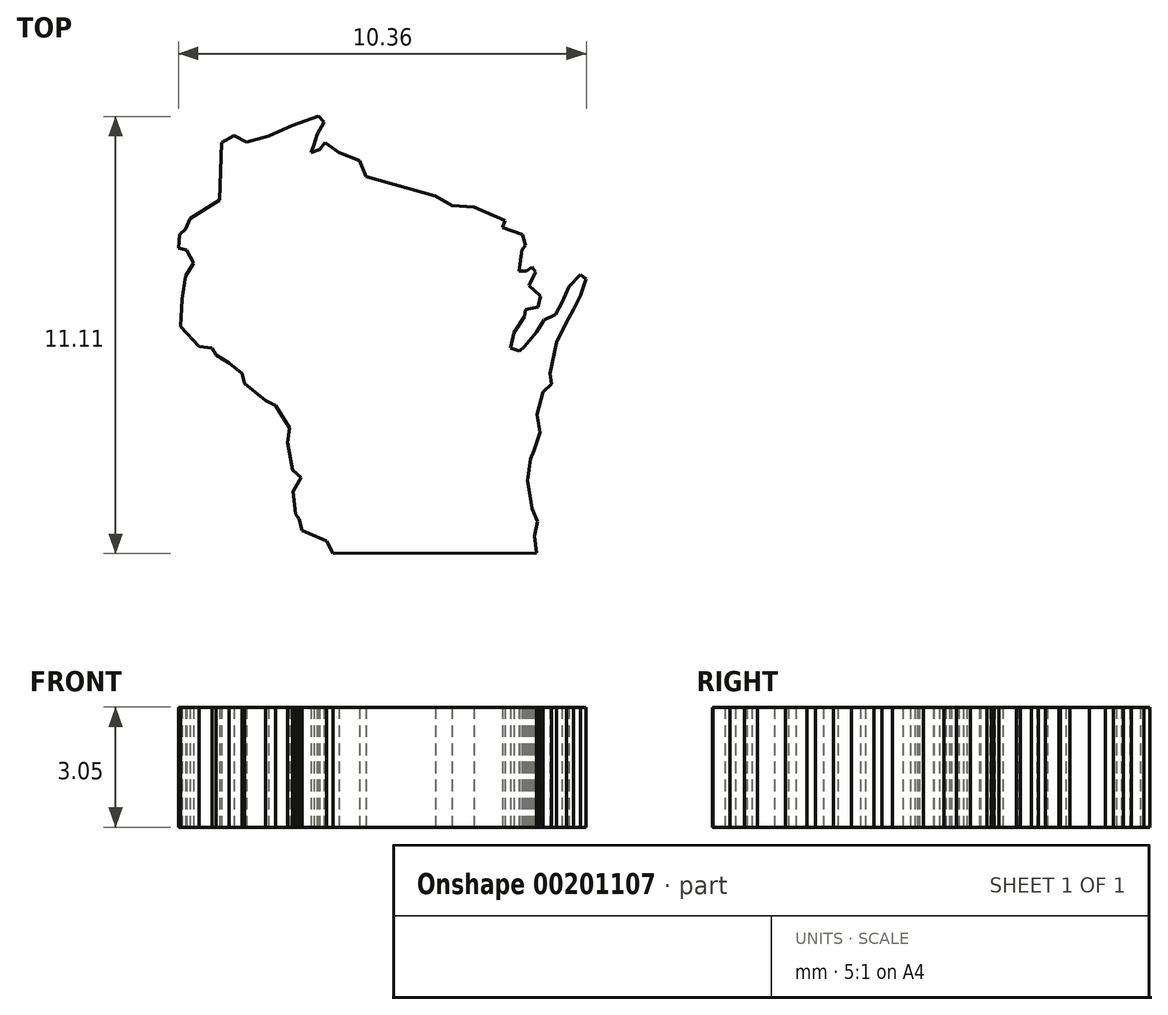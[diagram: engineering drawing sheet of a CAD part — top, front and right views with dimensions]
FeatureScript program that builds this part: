
annotation { "Feature Type Name" : "Feature", "Feature Type Description" : "" }
export const myFeature = defineFeature(function(context is Context, id is Id, definition is map)
    precondition{}
    {
        {
            var Q0;
            Q0=qCreatedBy(makeId("Top.planeOp"),FACE);
            var sketch = newSketch(context, id + "F0", { "sketchPlane" : qUnion([Q0])});
            skLineSegment(sketch, "E0", {"start": v(0.02, 0.02) * mm, "end": v(5.18, 0.03) * mm});
            skLineSegment(sketch, "E1", {"start": v(5.18, 0.03) * mm, "end": v(5.14, 0.47) * mm});
            skLineSegment(sketch, "E2", {"start": v(5.14, 0.47) * mm, "end": v(5.21, 0.84) * mm});
            skLineSegment(sketch, "E3", {"start": v(5.21, 0.84) * mm, "end": v(5.07, 1.17) * mm});
            skLineSegment(sketch, "E4", {"start": v(5.07, 1.17) * mm, "end": v(5.04, 1.34) * mm});
            skLineSegment(sketch, "E5", {"start": v(5.04, 1.34) * mm, "end": v(4.96, 1.87) * mm});
            skLineSegment(sketch, "E6", {"start": v(4.96, 1.87) * mm, "end": v(5.04, 2.42) * mm});
            skLineSegment(sketch, "E7", {"start": v(5.04, 2.42) * mm, "end": v(5.12, 2.64) * mm});
            skLineSegment(sketch, "E8", {"start": v(5.12, 2.64) * mm, "end": v(5.27, 3.1) * mm});
            skLineSegment(sketch, "E9", {"start": v(5.27, 3.1) * mm, "end": v(5.2, 3.55) * mm});
            skLineSegment(sketch, "E10", {"start": v(5.2, 3.55) * mm, "end": v(5.35, 4.12) * mm});
            skLineSegment(sketch, "E11", {"start": v(5.35, 4.12) * mm, "end": v(5.57, 4.32) * mm});
            skLineSegment(sketch, "E12", {"start": v(5.57, 4.32) * mm, "end": v(5.52, 4.6) * mm});
            skLineSegment(sketch, "E13", {"start": v(5.52, 4.6) * mm, "end": v(5.7, 5.38) * mm});
            skLineSegment(sketch, "E14", {"start": v(5.7, 5.38) * mm, "end": v(5.94, 5.9) * mm});
            skLineSegment(sketch, "E15", {"start": v(5.94, 5.9) * mm, "end": v(6.12, 6.22) * mm});
            skLineSegment(sketch, "E16", {"start": v(6.12, 6.22) * mm, "end": v(6.3, 6.58) * mm});
            skLineSegment(sketch, "E17", {"start": v(6.3, 6.58) * mm, "end": v(6.45, 7) * mm});
            skLineSegment(sketch, "E18", {"start": v(6.45, 7) * mm, "end": v(6.3, 7.1) * mm});
            skLineSegment(sketch, "E19", {"start": v(6.3, 7.1) * mm, "end": v(6, 6.8) * mm});
            skLineSegment(sketch, "E20", {"start": v(6, 6.8) * mm, "end": v(5.84, 6.4) * mm});
            skLineSegment(sketch, "E21", {"start": v(5.84, 6.4) * mm, "end": v(5.67, 6.1) * mm});
            skLineSegment(sketch, "E22", {"start": v(5.67, 6.1) * mm, "end": v(5.37, 5.95) * mm});
            skLineSegment(sketch, "E23", {"start": v(5.37, 5.95) * mm, "end": v(5.18, 5.65) * mm});
            skLineSegment(sketch, "E24", {"start": v(5.18, 5.65) * mm, "end": v(4.88, 5.29) * mm});
            skLineSegment(sketch, "E25", {"start": v(4.88, 5.29) * mm, "end": v(4.75, 5.17) * mm});
            skLineSegment(sketch, "E26", {"start": v(4.75, 5.17) * mm, "end": v(4.53, 5.25) * mm});
            skLineSegment(sketch, "E27", {"start": v(4.53, 5.25) * mm, "end": v(4.61, 5.63) * mm});
            skLineSegment(sketch, "E28", {"start": v(4.61, 5.63) * mm, "end": v(4.87, 6.04) * mm});
            skLineSegment(sketch, "E29", {"start": v(4.87, 6.04) * mm, "end": v(4.9, 6.22) * mm});
            skLineSegment(sketch, "E30", {"start": v(4.9, 6.22) * mm, "end": v(5.22, 6.29) * mm});
            skLineSegment(sketch, "E31", {"start": v(5.22, 6.29) * mm, "end": v(5.29, 6.57) * mm});
            skLineSegment(sketch, "E32", {"start": v(5.29, 6.57) * mm, "end": v(5, 6.83) * mm});
            skLineSegment(sketch, "E33", {"start": v(5, 6.83) * mm, "end": v(5.16, 7.18) * mm});
            skLineSegment(sketch, "E34", {"start": v(5.16, 7.18) * mm, "end": v(5.07, 7.3) * mm});
            skLineSegment(sketch, "E35", {"start": v(5.07, 7.3) * mm, "end": v(4.93, 7.2) * mm});
            skLineSegment(sketch, "E36", {"start": v(4.93, 7.2) * mm, "end": v(4.74, 7.2) * mm});
            skLineSegment(sketch, "E37", {"start": v(4.74, 7.2) * mm, "end": v(4.8, 7.74) * mm});
            skLineSegment(sketch, "E38", {"start": v(4.8, 7.74) * mm, "end": v(4.9, 7.84) * mm});
            skLineSegment(sketch, "E39", {"start": v(4.9, 7.84) * mm, "end": v(4.83, 8.13) * mm});
            skLineSegment(sketch, "E40", {"start": v(4.83, 8.13) * mm, "end": v(4.31, 8.3) * mm});
            skLineSegment(sketch, "E41", {"start": v(4.31, 8.3) * mm, "end": v(4.39, 8.49) * mm});
            skLineSegment(sketch, "E42", {"start": v(4.39, 8.49) * mm, "end": v(3.6, 8.82) * mm});
            skLineSegment(sketch, "E43", {"start": v(3.6, 8.82) * mm, "end": v(3.04, 8.86) * mm});
            skLineSegment(sketch, "E44", {"start": v(3.04, 8.86) * mm, "end": v(2.62, 9.1) * mm});
            skLineSegment(sketch, "E45", {"start": v(2.62, 9.1) * mm, "end": v(0.86, 9.6) * mm});
            skLineSegment(sketch, "E46", {"start": v(0.86, 9.6) * mm, "end": v(0.7, 10) * mm});
            skLineSegment(sketch, "E47", {"start": v(0.7, 10) * mm, "end": v(0.17, 10.2) * mm});
            skLineSegment(sketch, "E48", {"start": v(0.17, 10.2) * mm, "end": v(-0.18, 10.46) * mm});
            skLineSegment(sketch, "E49", {"start": v(-0.18, 10.46) * mm, "end": v(-0.33, 10.29) * mm});
            skLineSegment(sketch, "E50", {"start": v(-0.33, 10.29) * mm, "end": v(-0.54, 10.22) * mm});
            skLineSegment(sketch, "E51", {"start": v(-0.54, 10.22) * mm, "end": v(-0.47, 10.4) * mm});
            skLineSegment(sketch, "E52", {"start": v(-0.47, 10.4) * mm, "end": v(-0.4, 10.67) * mm});
            skLineSegment(sketch, "E53", {"start": v(-0.4, 10.67) * mm, "end": v(-0.2, 10.98) * mm});
            skLineSegment(sketch, "E54", {"start": v(-0.2, 10.98) * mm, "end": v(-0.35, 11.13) * mm});
            skLineSegment(sketch, "E55", {"start": v(-0.35, 11.13) * mm, "end": v(-1.02, 10.9) * mm});
            skLineSegment(sketch, "E56", {"start": v(-1.02, 10.9) * mm, "end": v(-1.63, 10.63) * mm});
            skLineSegment(sketch, "E57", {"start": v(-1.63, 10.63) * mm, "end": v(-2.19, 10.47) * mm});
            skLineSegment(sketch, "E58", {"start": v(-2.19, 10.47) * mm, "end": v(-2.5, 10.64) * mm});
            skLineSegment(sketch, "E59", {"start": v(-2.5, 10.64) * mm, "end": v(-2.82, 10.46) * mm});
            skLineSegment(sketch, "E60", {"start": v(-2.82, 10.46) * mm, "end": v(-2.87, 9) * mm});
            skLineSegment(sketch, "E61", {"start": v(-2.87, 9) * mm, "end": v(-3.62, 8.53) * mm});
            skLineSegment(sketch, "E62", {"start": v(-3.62, 8.53) * mm, "end": v(-3.73, 8.27) * mm});
            skLineSegment(sketch, "E63", {"start": v(-3.73, 8.27) * mm, "end": v(-3.88, 8.13) * mm});
            skLineSegment(sketch, "E64", {"start": v(-3.88, 8.13) * mm, "end": v(-3.91, 7.79) * mm});
            skLineSegment(sketch, "E65", {"start": v(-3.91, 7.79) * mm, "end": v(-3.7, 7.74) * mm});
            skLineSegment(sketch, "E66", {"start": v(-3.7, 7.74) * mm, "end": v(-3.52, 7.4) * mm});
            skLineSegment(sketch, "E67", {"start": v(-3.52, 7.4) * mm, "end": v(-3.73, 7.07) * mm});
            skLineSegment(sketch, "E68", {"start": v(-3.73, 7.07) * mm, "end": v(-3.82, 6.49) * mm});
            skLineSegment(sketch, "E69", {"start": v(-3.82, 6.49) * mm, "end": v(-3.85, 5.79) * mm});
            skLineSegment(sketch, "E70", {"start": v(-3.85, 5.79) * mm, "end": v(-3.39, 5.28) * mm});
            skLineSegment(sketch, "E71", {"start": v(-3.39, 5.28) * mm, "end": v(-3.06, 5.24) * mm});
            skLineSegment(sketch, "E72", {"start": v(-3.06, 5.24) * mm, "end": v(-2.96, 5.06) * mm});
            skLineSegment(sketch, "E73", {"start": v(-2.96, 5.06) * mm, "end": v(-2.63, 4.86) * mm});
            skLineSegment(sketch, "E74", {"start": v(-2.63, 4.86) * mm, "end": v(-2.3, 4.6) * mm});
            skLineSegment(sketch, "E75", {"start": v(-2.3, 4.6) * mm, "end": v(-2.23, 4.34) * mm});
            skLineSegment(sketch, "E76", {"start": v(-2.23, 4.34) * mm, "end": v(-1.7, 3.9) * mm});
            skLineSegment(sketch, "E77", {"start": v(-1.7, 3.9) * mm, "end": v(-1.45, 3.79) * mm});
            skLineSegment(sketch, "E78", {"start": v(-1.45, 3.79) * mm, "end": v(-1.1, 3.22) * mm});
            skLineSegment(sketch, "E79", {"start": v(-1.1, 3.22) * mm, "end": v(-1.14, 2.85) * mm});
            skLineSegment(sketch, "E80", {"start": v(-1.14, 2.85) * mm, "end": v(-1.02, 2.14) * mm});
            skLineSegment(sketch, "E81", {"start": v(-1.02, 2.14) * mm, "end": v(-0.8, 1.96) * mm});
            skLineSegment(sketch, "E82", {"start": v(-0.8, 1.96) * mm, "end": v(-1, 1.6) * mm});
            skLineSegment(sketch, "E83", {"start": v(-1, 1.6) * mm, "end": v(-0.94, 1.03) * mm});
            skLineSegment(sketch, "E84", {"start": v(-0.94, 1.03) * mm, "end": v(-0.85, 0.9) * mm});
            skLineSegment(sketch, "E85", {"start": v(-0.85, 0.9) * mm, "end": v(-0.78, 0.6) * mm});
            skLineSegment(sketch, "E86", {"start": v(-0.78, 0.6) * mm, "end": v(-0.15, 0.34) * mm});
            skLineSegment(sketch, "E87", {"start": v(-0.15, 0.34) * mm, "end": v(0.02, 0.02) * mm});
            skSolve(sketch);
        }
        {
            var Q0;
            Q0=makeQuery(id+"F0.imprint","IMPRINT",FACE,{"disambiguationData":[TD([[makeQuery(id+"F0.imprint","IMPRINT",EDGE,{"derivedFrom":sQuery(id+"F0.wireOp",EDGE,"E0")}),1.0]])]});
            var Q1;
            Q1=sQuery(id+"F0.wireOp",EDGE,"E45");
            var Q2;
            Q2=sQuery(id+"F0.wireOp",EDGE,"E0");
            var Q3;
            Q3=sQuery(id+"F0.wireOp",EDGE,"E58");
            var Q4;
            Q4=sQuery(id+"F0.wireOp",EDGE,"E42");
            var Q5;
            Q5=sQuery(id+"F0.wireOp",EDGE,"E74");
            var Q6;
            Q6=sQuery(id+"F0.wireOp",EDGE,"E83");
            var Q7;
            Q7=sQuery(id+"F0.wireOp",EDGE,"E59");
            var Q8;
            Q8=sQuery(id+"F0.wireOp",EDGE,"E43");
            var Q9;
            Q9=sQuery(id+"F0.wireOp",EDGE,"E75");
            var Q10;
            Q10=sQuery(id+"F0.wireOp",EDGE,"E77");
            var Q11;
            Q11=sQuery(id+"F0.wireOp",EDGE,"E84");
            var Q12;
            Q12=sQuery(id+"F0.wireOp",EDGE,"E61");
            var Q13;
            Q13=sQuery(id+"F0.wireOp",EDGE,"E68");
            var Q14;
            Q14=sQuery(id+"F0.wireOp",EDGE,"E60");
            var Q15;
            Q15=sQuery(id+"F0.wireOp",EDGE,"E44");
            var Q16;
            Q16=sQuery(id+"F0.wireOp",EDGE,"E76");
            var Q17;
            Q17=sQuery(id+"F0.wireOp",EDGE,"E78");
            var Q18;
            Q18=sQuery(id+"F0.wireOp",EDGE,"E85");
            var Q19;
            Q19=sQuery(id+"F0.wireOp",EDGE,"E69");
            var Q20;
            Q20=sQuery(id+"F0.wireOp",EDGE,"E46");
            var Q21;
            Q21=sQuery(id+"F0.wireOp",EDGE,"E86");
            var Q22;
            Q22=sQuery(id+"F0.wireOp",EDGE,"E79");
            var Q23;
            Q23=sQuery(id+"F0.wireOp",EDGE,"E70");
            var Q24;
            Q24=sQuery(id+"F0.wireOp",EDGE,"E47");
            var Q25;
            Q25=sQuery(id+"F0.wireOp",EDGE,"E13");
            var Q26;
            Q26=sQuery(id+"F0.wireOp",EDGE,"E1");
            var Q27;
            Q27=sQuery(id+"F0.wireOp",EDGE,"E2");
            var Q28;
            Q28=sQuery(id+"F0.wireOp",EDGE,"E3");
            var Q29;
            Q29=sQuery(id+"F0.wireOp",EDGE,"E4");
            var Q30;
            Q30=sQuery(id+"F0.wireOp",EDGE,"E5");
            var Q31;
            Q31=sQuery(id+"F0.wireOp",EDGE,"E6");
            var Q32;
            Q32=sQuery(id+"F0.wireOp",EDGE,"E7");
            var Q33;
            Q33=sQuery(id+"F0.wireOp",EDGE,"E8");
            var Q34;
            Q34=sQuery(id+"F0.wireOp",EDGE,"E9");
            var Q35;
            Q35=sQuery(id+"F0.wireOp",EDGE,"E10");
            var Q36;
            Q36=sQuery(id+"F0.wireOp",EDGE,"E87");
            var Q37;
            Q37=sQuery(id+"F0.wireOp",EDGE,"E71");
            var Q38;
            Q38=sQuery(id+"F0.wireOp",EDGE,"E80");
            var Q39;
            Q39=sQuery(id+"F0.wireOp",EDGE,"E56");
            var Q40;
            Q40=sQuery(id+"F0.wireOp",EDGE,"E72");
            var Q41;
            Q41=sQuery(id+"F0.wireOp",EDGE,"E81");
            var Q42;
            Q42=sQuery(id+"F0.wireOp",EDGE,"E57");
            var Q43;
            Q43=sQuery(id+"F0.wireOp",EDGE,"E41");
            var Q44;
            Q44=sQuery(id+"F0.wireOp",EDGE,"E73");
            var Q45;
            Q45=sQuery(id+"F0.wireOp",EDGE,"E18");
            var Q46;
            Q46=sQuery(id+"F0.wireOp",EDGE,"E82");
            var Q47;
            Q47=sQuery(id+"F0.wireOp",EDGE,"E19");
            var Q48;
            Q48=sQuery(id+"F0.wireOp",EDGE,"E67");
            var Q49;
            Q49=sQuery(id+"F0.wireOp",EDGE,"E20");
            var Q50;
            Q50=sQuery(id+"F0.wireOp",EDGE,"E62");
            var Q51;
            Q51=sQuery(id+"F0.wireOp",EDGE,"E11");
            var Q52;
            Q52=sQuery(id+"F0.wireOp",EDGE,"E12");
            var Q53;
            Q53=sQuery(id+"F0.wireOp",EDGE,"E55");
            var Q54;
            Q54=sQuery(id+"F0.wireOp",EDGE,"E39");
            var Q55;
            Q55=sQuery(id+"F0.wireOp",EDGE,"E16");
            var Q56;
            Q56=sQuery(id+"F0.wireOp",EDGE,"E40");
            var Q57;
            Q57=sQuery(id+"F0.wireOp",EDGE,"E17");
            var Q58;
            Q58=sQuery(id+"F0.wireOp",EDGE,"E26");
            var Q59;
            Q59=sQuery(id+"F0.wireOp",EDGE,"E27");
            var Q60;
            Q60=sQuery(id+"F0.wireOp",EDGE,"E52");
            var Q61;
            Q61=sQuery(id+"F0.wireOp",EDGE,"E36");
            var Q62;
            Q62=sQuery(id+"F0.wireOp",EDGE,"E53");
            var Q63;
            Q63=sQuery(id+"F0.wireOp",EDGE,"E37");
            var Q64;
            Q64=sQuery(id+"F0.wireOp",EDGE,"E63");
            var Q65;
            Q65=sQuery(id+"F0.wireOp",EDGE,"E54");
            var Q66;
            Q66=sQuery(id+"F0.wireOp",EDGE,"E38");
            var Q67;
            Q67=sQuery(id+"F0.wireOp",EDGE,"E14");
            var Q68;
            Q68=sQuery(id+"F0.wireOp",EDGE,"E15");
            var Q69;
            Q69=sQuery(id+"F0.wireOp",EDGE,"E48");
            var Q70;
            Q70=sQuery(id+"F0.wireOp",EDGE,"E64");
            var Q71;
            Q71=sQuery(id+"F0.wireOp",EDGE,"E24");
            var Q72;
            Q72=sQuery(id+"F0.wireOp",EDGE,"E65");
            var Q73;
            Q73=sQuery(id+"F0.wireOp",EDGE,"E49");
            var Q74;
            Q74=sQuery(id+"F0.wireOp",EDGE,"E33");
            var Q75;
            Q75=sQuery(id+"F0.wireOp",EDGE,"E25");
            var Q76;
            Q76=sQuery(id+"F0.wireOp",EDGE,"E66");
            var Q77;
            Q77=sQuery(id+"F0.wireOp",EDGE,"E50");
            var Q78;
            Q78=sQuery(id+"F0.wireOp",EDGE,"E34");
            var Q79;
            Q79=sQuery(id+"F0.wireOp",EDGE,"E51");
            var Q80;
            Q80=sQuery(id+"F0.wireOp",EDGE,"E35");
            var Q81;
            Q81=sQuery(id+"F0.wireOp",EDGE,"E29");
            var Q82;
            Q82=sQuery(id+"F0.wireOp",EDGE,"E28");
            var Q83;
            Q83=sQuery(id+"F0.wireOp",EDGE,"E21");
            var Q84;
            Q84=sQuery(id+"F0.wireOp",EDGE,"E30");
            var Q85;
            Q85=sQuery(id+"F0.wireOp",EDGE,"E22");
            var Q86;
            Q86=sQuery(id+"F0.wireOp",EDGE,"E31");
            var Q87;
            Q87=sQuery(id+"F0.wireOp",EDGE,"E23");
            var Q88;
            Q88=sQuery(id+"F0.wireOp",EDGE,"E32");
            extrude(context, id + "F1", {"entities" : qUnion([Q0]), "surfaceEntities" : qUnion([Q1, Q2, Q3, Q4, Q5, Q6, Q7, Q8, Q9, Q10, Q11, Q12, Q13, Q14, Q15, Q16, Q17, Q18, Q19, Q20, Q21, Q22, Q23, Q24, Q25, Q26, Q27, Q28, Q29, Q30, Q31, Q32, Q33, Q34, Q35, Q36, Q37, Q38, Q39, Q40, Q41, Q42, Q43, Q44, Q45, Q46, Q47, Q48, Q49, Q50, Q51, Q52, Q53, Q54, Q55, Q56, Q57, Q58, Q59, Q60, Q61, Q62, Q63, Q64, Q65, Q66, Q67, Q68, Q69, Q70, Q71, Q72, Q73, Q74, Q75, Q76, Q77, Q78, Q79, Q80, Q81, Q82, Q83, Q84, Q85, Q86, Q87, Q88]), "depth" : 3.05 * mm});
        }
    });
